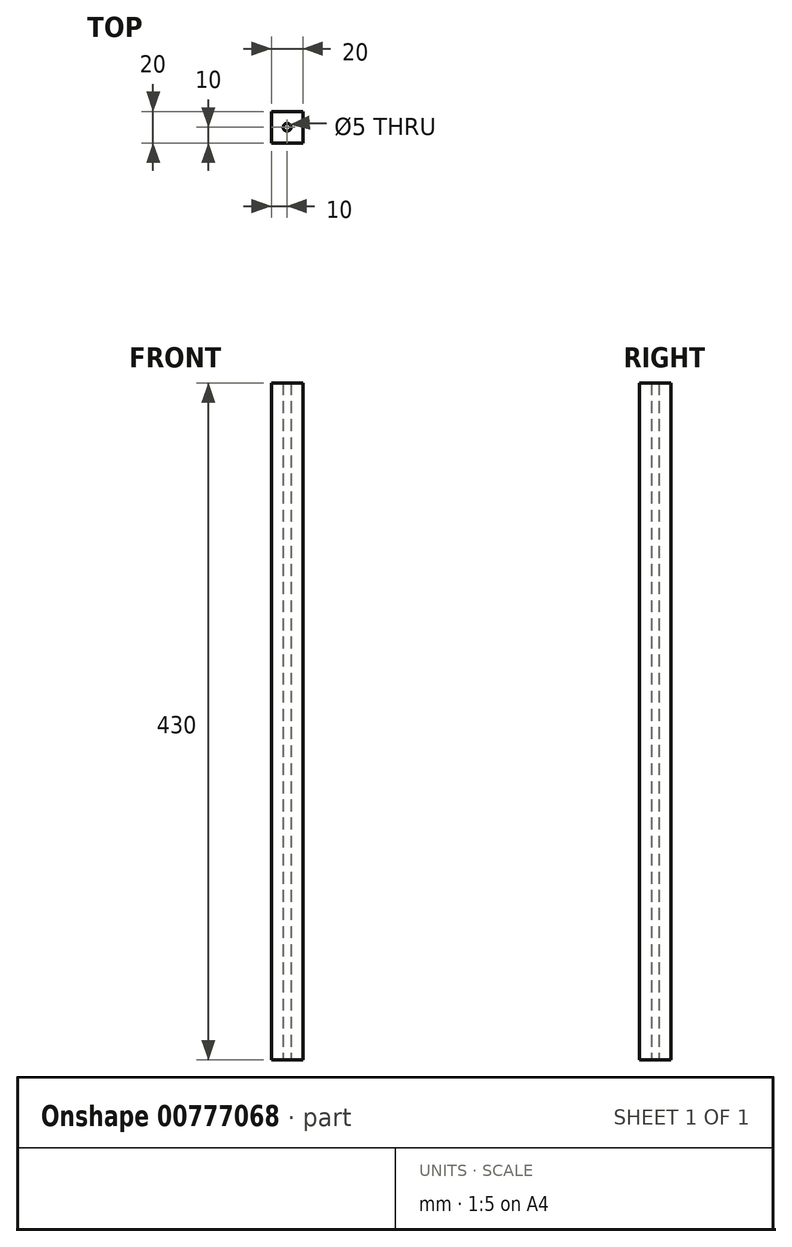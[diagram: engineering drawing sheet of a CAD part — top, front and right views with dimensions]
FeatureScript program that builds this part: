
annotation { "Feature Type Name" : "Feature", "Feature Type Description" : "" }
export const myFeature = defineFeature(function(context is Context, id is Id, definition is map)
    precondition{}
    {
        {
            var Q0;
            Q0=qCreatedBy(makeId("Top.planeOp"),FACE);
            var sketch = newSketch(context, id + "F0", { "sketchPlane" : qUnion([Q0])});
            skLineSegment(sketch, "E0.bottom", {"start": v(-10, 10) * mm, "end": v(10, 10) * mm});
            skLineSegment(sketch, "E0.top", {"start": v(-10, -10) * mm, "end": v(10, -10) * mm});
            skLineSegment(sketch, "E0.left", {"start": v(-10, 10) * mm, "end": v(-10, -10) * mm});
            skLineSegment(sketch, "E0.right", {"start": v(10, 10) * mm, "end": v(10, -10) * mm});
            skCircle(sketch, "E1", {"center": v(0, 0) * mm, "radius": 2.5 * mm});
            skSolve(sketch);
        }
        {
            var Q0;
            Q0=qSketchRegion(id+"F0",true);
            extrude(context, id + "F1", {"entities" : qUnion([Q0]), "depth" : (480 - 50) * mm, "offsetDistance" : 25 * mm});
        }
    });
